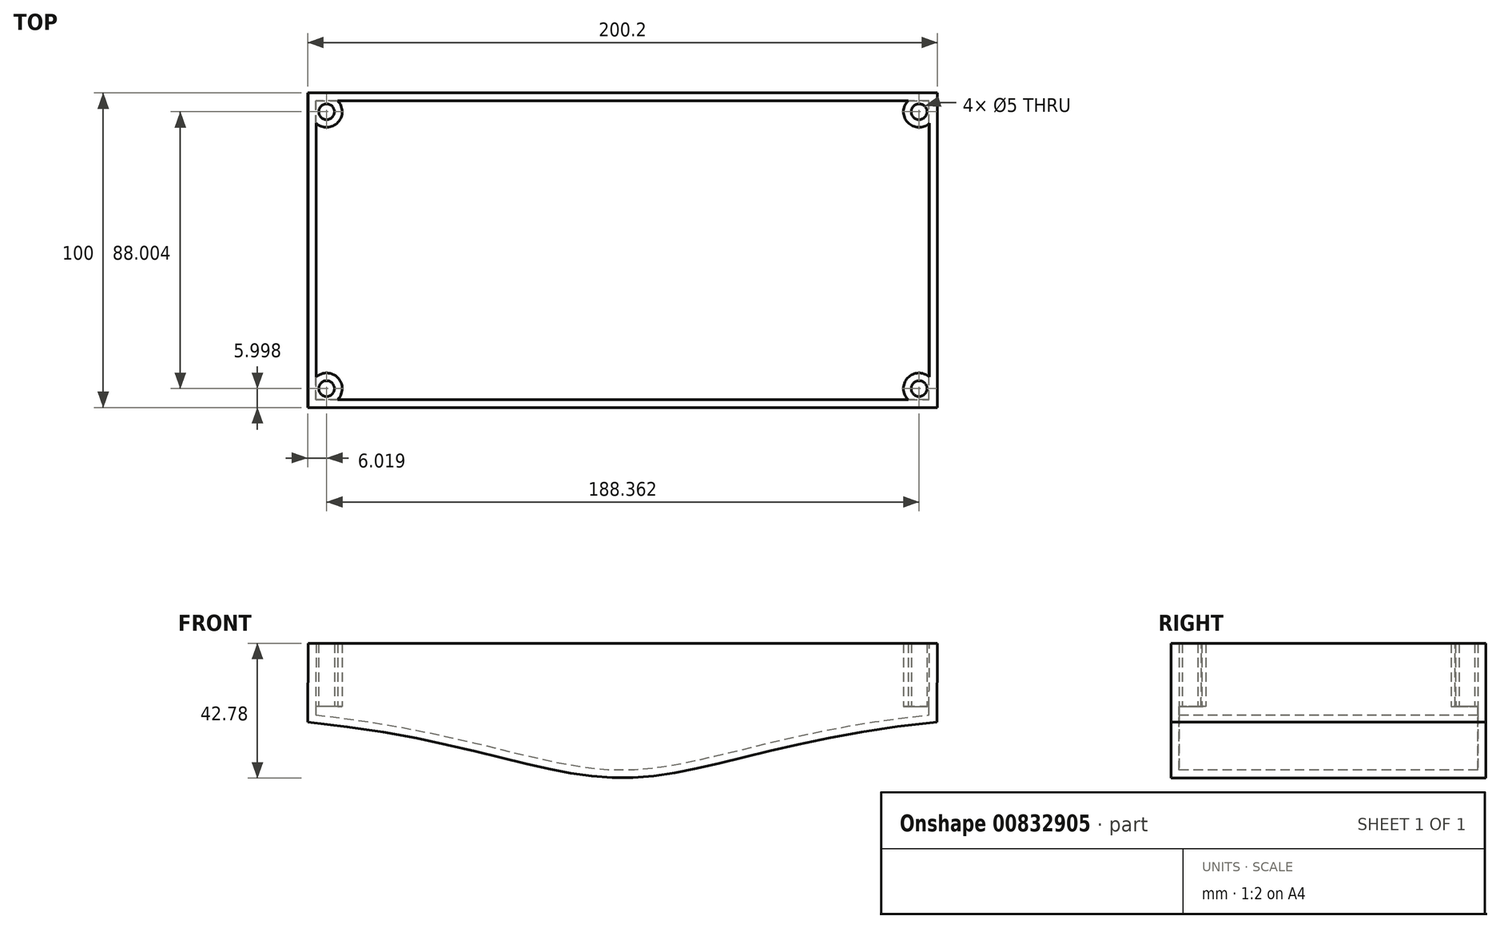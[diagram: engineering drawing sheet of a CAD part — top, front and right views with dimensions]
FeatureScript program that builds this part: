
annotation { "Feature Type Name" : "Feature", "Feature Type Description" : "" }
export const myFeature = defineFeature(function(context is Context, id is Id, definition is map)
    precondition{}
    {
        {
            var Q0;
            Q0=qCreatedBy(makeId("Front.planeOp"),FACE);
            var sketch = newSketch(context, id + "F0", { "sketchPlane" : qUnion([Q0])});
            skLineSegment(sketch, "E0.bottom", {"start": v(-100, 20) * mm, "end": v(100, 20) * mm});
            skLineSegment(sketch, "E0.left", {"start": v(-100, 20) * mm, "end": v(-100.2, -5) * mm});
            skFitSpline(sketch, "E1", {"points": [v(-100.2, -5) * mm, v(0, -22.78) * mm, v(99.8, -5) * mm], "startDerivative": vector(300.9, -30.06) * mm, "endDerivative": vector(299.1, 28.6) * mm});
            skLineSegment(sketch, "E2", {"start": v(99.8, -5) * mm, "end": v(100, 20) * mm});
            skSolve(sketch);
        }
        {
            var Q0;
            Q0=makeQuery(id+"F0.imprint","IMPRINT",FACE,{"disambiguationData":[TD([[makeQuery(id+"F0.imprint","IMPRINT",EDGE,{"derivedFrom":sQuery(id+"F0.wireOp",EDGE,"E0.bottom")}),-1.0]])]});
            extrude(context, id + "F1", {"entities" : qUnion([Q0]), "endBound" : BoundingType.SYMMETRIC, "depth" : 100 * mm, "offsetDistance" : 25 * mm});
        }
        {
            var Q0;
            Q0=makeQuery(id+"F1.opExtrude","SWEPT_FACE",FACE,{"disambiguationData":[OSD([sQuery(id+"F0.wireOp",EDGE,"E0.bottom")])]});
            shell(context, id + "F2", {"entities" : qUnion([Q0]), "thickness" : 2.5 * mm});
        }
        {
            var Q0;
            Q0=qCreatedBy(makeId("Top.planeOp"),FACE);
            var sketch = newSketch(context, id + "F3", { "sketchPlane" : qUnion([Q0])});
            skCircle(sketch, "E3", {"center": v(-94.18, -44) * mm, "radius": 4.96 * mm});
            skCircle(sketch, "E4", {"center": v(-94.18, -44) * mm, "radius": 2.5 * mm});
            skSolve(sketch);
        }
        {
            var Q0;
            Q0=makeQuery(id+"F3.imprint","IMPRINT",FACE,{"disambiguationData":[TD([[makeQuery(id+"F3.imprint","IMPRINT",EDGE,{"derivedFrom":sQuery(id+"F3.wireOp",EDGE,"E3")}),1.0]])]});
            extrude(context, id + "F4", {"entities" : qUnion([Q0]), "depth" : 20 * mm, "offsetDistance" : 25 * mm});
        }
        {
            var Q0;
            Q0=makeQuery(id+"F4.opExtrude","SWEPT_BODY",BODY,{"disambiguationData":[OSD([sQuery(id+"F3.wireOp",EDGE,"E3"),sQuery(id+"F3.wireOp",EDGE,"E4")])]});
            var Q1;
            Q1=qCreatedBy(makeId("Right.planeOp"),FACE);
            mirror(context, id + "F5", {"entities" : qUnion([Q0]), "mirrorPlane" : qUnion([Q1])});
        }
        {
            var Q0;
            Q0=makeQuery(id+"F4.opExtrude","SWEPT_BODY",BODY,{"disambiguationData":[OSD([sQuery(id+"F3.wireOp",EDGE,"E3"),sQuery(id+"F3.wireOp",EDGE,"E4")])]});
            var Q1;
            Q1=makeQuery(id+"F5.opPattern","COPY",BODY,{"derivedFrom":makeQuery(id+"F4.opExtrude","SWEPT_BODY",BODY,{"disambiguationData":[OSD([sQuery(id+"F3.wireOp",EDGE,"E3"),sQuery(id+"F3.wireOp",EDGE,"E4")])]}),"instanceName":"1"});
            var Q2;
            Q2=qCreatedBy(makeId("Front.planeOp"),FACE);
            mirror(context, id + "F6", {"operationType" : NewBodyOperationType.ADD, "entities" : qUnion([Q0, Q1]), "mirrorPlane" : qUnion([Q2])});
        }
    });
